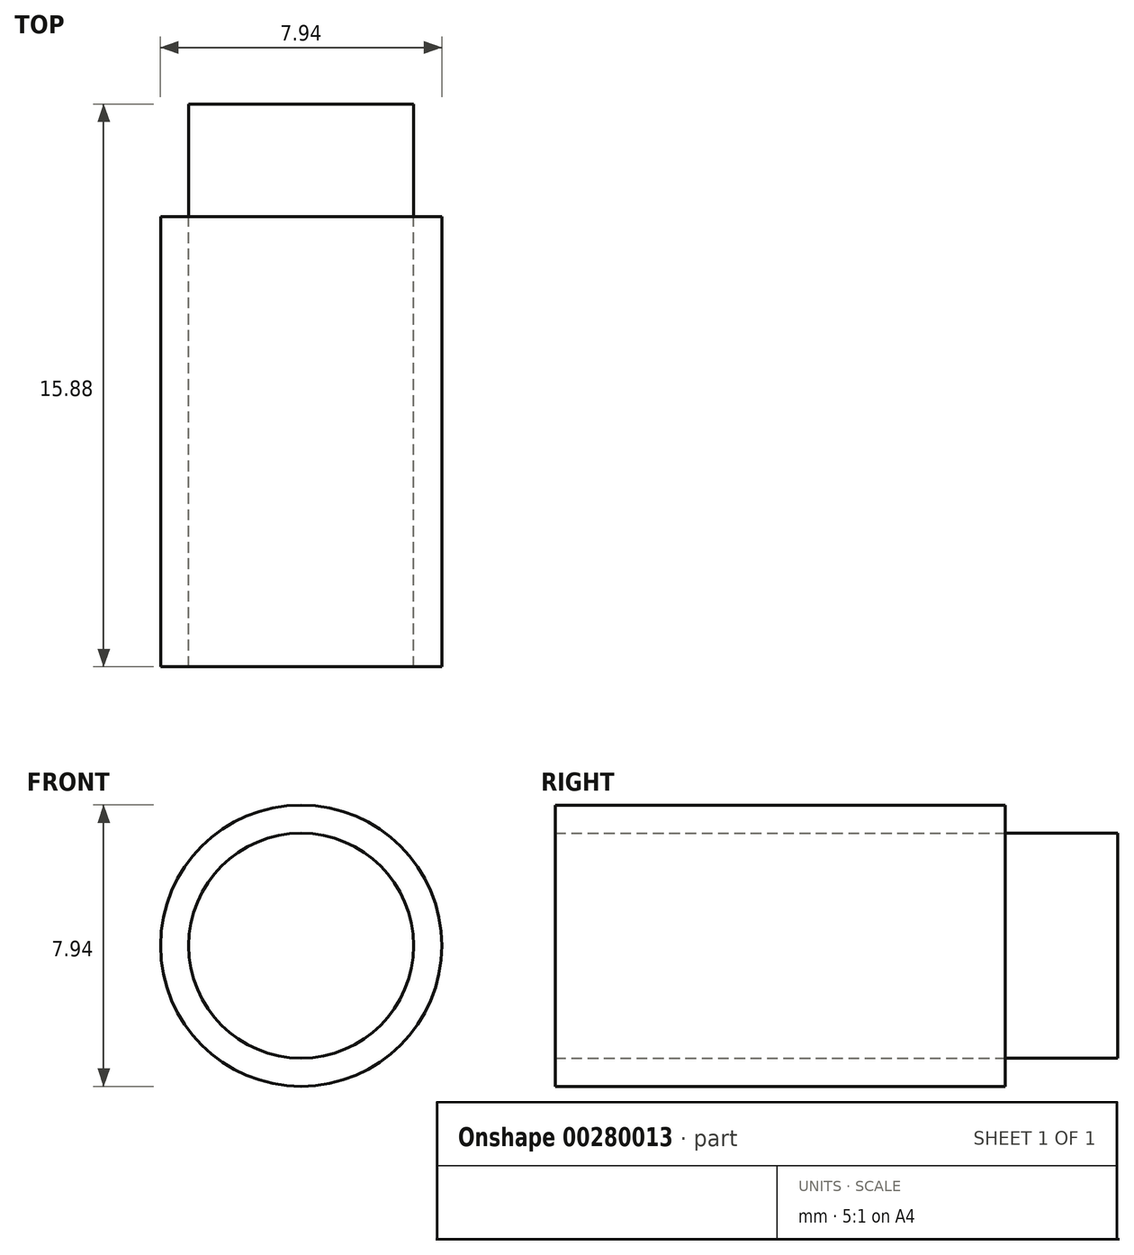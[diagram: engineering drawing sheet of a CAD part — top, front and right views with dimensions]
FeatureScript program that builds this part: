
annotation { "Feature Type Name" : "Feature", "Feature Type Description" : "" }
export const myFeature = defineFeature(function(context is Context, id is Id, definition is map)
    precondition{}
    {
        {
            var Q0;
            Q0=qCreatedBy(makeId("Front.planeOp"),FACE);
            var sketch = newSketch(context, id + "F0", { "sketchPlane" : qUnion([Q0])});
            skCircle(sketch, "E0", {"center": v(0, 0) * mm, "radius": 3.97 * mm});
            skCircle(sketch, "E1", {"center": v(0, 0) * mm, "radius": 3.18 * mm});
            skSolve(sketch);
        }
        {
            var Q0;
            Q0 = qSketchRegion(id + "F0", true);
            extrude(context, id + "F1", {"entities" : qUnion([Q0]), "depth" : 12.7 * mm});
        }
        {
            var Q0;
            Q0=makeQuery(id+"F1.opExtrude","CAP_FACE",FACE,{"disambiguationData":[OSD([sQuery(id+"F0.wireOp",EDGE,"E0"),sQuery(id+"F0.wireOp",EDGE,"E1")])],"isStart":true});
            var sketch = newSketch(context, id + "F2", { "sketchPlane" : qUnion([Q0])});
            skCircle(sketch, "E2", {"center": v(0, 0) * mm, "radius": 3.18 * mm});
            skSolve(sketch);
        }
        {
            var Q0;
            Q0 = qSketchRegion(id + "F2", true);
            extrude(context, id + "F3", {"entities" : qUnion([Q0]), "depth" : 3.17 * mm});
        }
    });
